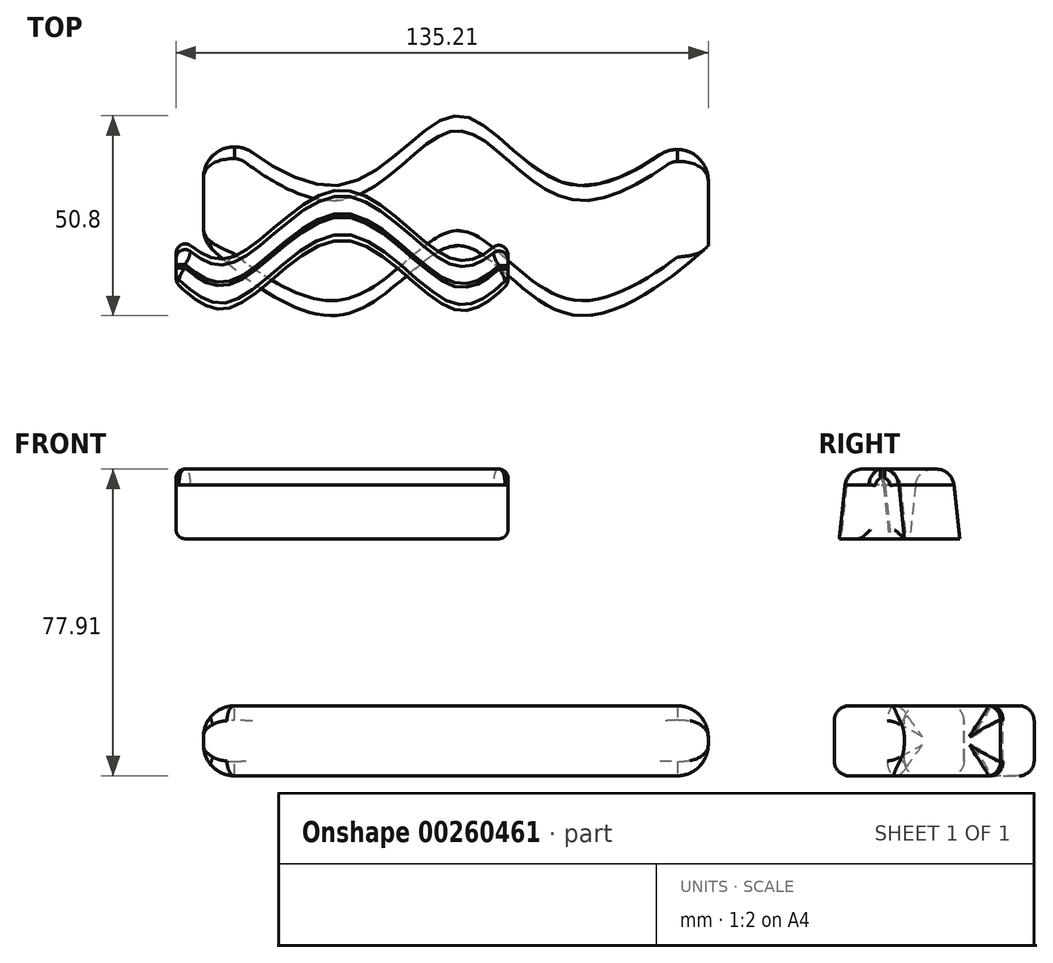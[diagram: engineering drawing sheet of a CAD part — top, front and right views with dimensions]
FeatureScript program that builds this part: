
annotation { "Feature Type Name" : "Feature", "Feature Type Description" : "" }
export const myFeature = defineFeature(function(context is Context, id is Id, definition is map)
    precondition{}
    {
        {
            var Q0;
            Q0=qCreatedBy(makeId("Top.planeOp"),FACE);
            var sketch = newSketch(context, id + "F0", { "sketchPlane" : qUnion([Q0])});
            skLineSegment(sketch, "E0", {"start": v(-76.12, 17.78) * mm, "end": v(-12.62, 17.78) * mm});
            skLineSegment(sketch, "E1", {"start": v(-44.37, 0) * mm, "end": v(19.13, 0) * mm});
            skLineSegment(sketch, "E2", {"start": v(-44.37, 0) * mm, "end": v(-44.37, 17.78) * mm});
            skLineSegment(sketch, "E3", {"start": v(-12.62, 17.78) * mm, "end": v(-12.62, 0) * mm});
            skLineSegment(sketch, "E4", {"start": v(-12.62, 8.9) * mm, "end": v(-44.37, 8.89) * mm});
            skLineSegment(sketch, "E5", {"start": v(-12.62, 17.78) * mm, "end": v(50.88, 17.78) * mm});
            skFitSpline(sketch, "E6", {"points": [v(-77.36, 17.78) * mm, v(-76.12, 17.78) * mm, v(-44.37, 0) * mm, v(-12.62, 17.78) * mm, v(19.13, 0) * mm, v(50.88, 17.78) * mm], "startDerivative": vector(84.4, 0) * mm, "endDerivative": vector(0, 0) * mm});
            skSolve(sketch);
        }
        {
            var Q0;
            Q0=qCreatedBy(makeId("Right.planeOp"),FACE);
            var sketch = newSketch(context, id + "F1", { "sketchPlane" : qUnion([Q0])});
            skLineSegment(sketch, "E7.bottom", {"start": v(-3.81, -40.82) * mm, "end": v(-29.21, -40.82) * mm});
            skLineSegment(sketch, "E7.top", {"start": v(-3.8, -58.6) * mm, "end": v(-29.21, -58.6) * mm});
            skLineSegment(sketch, "E7.left", {"start": v(0, -44.63) * mm, "end": v(0, -54.8) * mm});
            skLineSegment(sketch, "E7.right", {"start": v(-33.02, -44.63) * mm, "end": v(-33.02, -54.8) * mm});
            skPoint(sketch, "E7.middle", {"position": v(-16.51, -49.71) * mm});
            skPoint(sketch, "E8.visualSharp", {"position": v(0, -58.6) * mm});
            skArc(sketch, "E8.filletArc", {"start": v(-3.8, -58.6) * mm, "mid": v(-1.12, -57.49) * mm, "end": v(0, -54.8) * mm});
            skPoint(sketch, "E9.visualSharp", {"position": v(-33.02, -58.6) * mm});
            skArc(sketch, "E9.filletArc", {"start": v(-33.02, -54.8) * mm, "mid": v(-31.9, -57.49) * mm, "end": v(-29.21, -58.6) * mm});
            skPoint(sketch, "E10.visualSharp", {"position": v(-33.02, -40.82) * mm});
            skArc(sketch, "E10.filletArc", {"start": v(-29.21, -40.82) * mm, "mid": v(-31.9, -41.94) * mm, "end": v(-33.02, -44.63) * mm});
            skPoint(sketch, "E11.visualSharp", {"position": v(0, -40.82) * mm});
            skArc(sketch, "E11.filletArc", {"start": v(0, -44.63) * mm, "mid": v(-1.12, -41.94) * mm, "end": v(-3.81, -40.82) * mm});
            skSolve(sketch);
        }
        {
            var Q0;
            Q0=makeQuery(id+"F1.imprint","IMPRINT",FACE,{"disambiguationData":[TD([[makeQuery(id+"F1.imprint","IMPRINT",EDGE,{"derivedFrom":sQuery(id+"F1.wireOp",EDGE,"E7.bottom")}),1.0]])]});
            var Q1;
            Q1=sQuery(id+"F0.wireOp",EDGE,"E6");
            sweep(context, id + "F2", {"profiles" : qUnion([Q0]), "path" : qUnion([Q1]), "keepProfileOrientation" : true});
        }
        {
            var Q0;
            Q0=makeQuery(id+"F2.opSweep","CAP_FACE",FACE,{"disambiguationData":[OSD([sQuery(id+"F0.wireOp",VERTEX,"E6.start"),sQuery(id+"F1.wireOp",EDGE,"E7.bottom"),sQuery(id+"F1.wireOp",EDGE,"E7.top"),sQuery(id+"F1.wireOp",EDGE,"E7.left"),sQuery(id+"F1.wireOp",EDGE,"E7.right"),sQuery(id+"F1.wireOp",EDGE,"E8.filletArc"),sQuery(id+"F1.wireOp",EDGE,"E9.filletArc"),sQuery(id+"F1.wireOp",EDGE,"E10.filletArc"),sQuery(id+"F1.wireOp",EDGE,"E11.filletArc")])],"isStart":false});
            var Q1;
            Q1=makeQuery(id+"F2.opSweep","CAP_FACE",FACE,{"disambiguationData":[OSD([sQuery(id+"F0.wireOp",VERTEX,"E6.end"),sQuery(id+"F1.wireOp",EDGE,"E7.bottom"),sQuery(id+"F1.wireOp",EDGE,"E7.top"),sQuery(id+"F1.wireOp",EDGE,"E7.left"),sQuery(id+"F1.wireOp",EDGE,"E7.right"),sQuery(id+"F1.wireOp",EDGE,"E8.filletArc"),sQuery(id+"F1.wireOp",EDGE,"E9.filletArc"),sQuery(id+"F1.wireOp",EDGE,"E10.filletArc"),sQuery(id+"F1.wireOp",EDGE,"E11.filletArc")])],"isStart":true});
            fillet(context, id + "F3", {"entities" : qUnion([Q0, Q1]), "radius" : 7.87 * mm, "tangentPropagation" : true, "allowEdgeOverflow" : false});
        }
        {
            var Q0;
            Q0=makeQuery(id+"F2.opSweep","SWEPT_FACE",FACE,{"disambiguationData":[OSD([sQuery(id+"F0.wireOp",EDGE,"E6"),sQuery(id+"F1.wireOp",EDGE,"E7.top")])]});
            var sketch = newSketch(context, id + "F4", { "sketchPlane" : qUnion([Q0])});
            skLineSegment(sketch, "E12", {"start": v(-120.37, 23.01) * mm, "end": v(-7.87, 23.01) * mm});
            skLineSegment(sketch, "E13", {"start": v(-64.12, 23.01) * mm, "end": v(-64.12, 3.83) * mm});
            skPoint(sketch, "E14", {"position": v(-92.25, 23.01) * mm});
            skPoint(sketch, "E15", {"position": v(-36, 23.01) * mm});
            skLineSegment(sketch, "E16", {"start": v(-120.37, 35.1) * mm, "end": v(-7.87, 35.93) * mm});
            skLineSegment(sketch, "E17", {"start": v(-92.25, 23.01) * mm, "end": v(-92.25, 35.31) * mm});
            skLineSegment(sketch, "E18", {"start": v(-36, 23.01) * mm, "end": v(-36, 35.73) * mm});
            skPoint(sketch, "E19", {"position": v(-106.3, 23.01) * mm});
            skPoint(sketch, "E20", {"position": v(-21.93, 23.01) * mm});
            skLineSegment(sketch, "E21", {"start": v(-21.93, 23.01) * mm, "end": v(-22.03, 35.83) * mm});
            skLineSegment(sketch, "E22", {"start": v(-106.3, 23.01) * mm, "end": v(-106.3, 35.2) * mm});
            skPoint(sketch, "E23", {"position": v(-106.3, 29.1) * mm});
            skPoint(sketch, "E24", {"position": v(-21.98, 29.42) * mm});
            skPoint(sketch, "E25", {"position": v(-64.12, 13.42) * mm});
            skLineSegment(sketch, "E26", {"start": v(-64.12, 13.42) * mm, "end": v(-64.12, 23.01) * mm});
            skPoint(sketch, "E27", {"position": v(-64.12, 18.22) * mm});
            skFitSpline(sketch, "E28", {"points": [v(-106.3, 29.1) * mm, v(-92.25, 35.31) * mm, v(-64.12, 18.22) * mm, v(-36, 35.73) * mm, v(-21.98, 29.42) * mm], "startDerivative": vector(64.15, 58.57) * mm, "endDerivative": vector(63.99, -59.4) * mm});
            skSolve(sketch);
        }
        {
            var Q0;
            Q0=qCreatedBy(makeId("Right.planeOp"),FACE);
            var sketch = newSketch(context, id + "F5", { "sketchPlane" : qUnion([Q0])});
            skLineSegment(sketch, "E29", {"start": v(-22.58, 1.63) * mm, "end": v(-35.28, 1.63) * mm});
            skLineSegment(sketch, "E30", {"start": v(-28.48, 19.3) * mm, "end": v(-29.39, 19.3) * mm});
            skLineSegment(sketch, "E31", {"start": v(-24.06, 15.34) * mm, "end": v(-22.58, 1.63) * mm});
            skLineSegment(sketch, "E32", {"start": v(-33.8, 15.34) * mm, "end": v(-35.28, 1.63) * mm});
            skPoint(sketch, "E33.visualSharp", {"position": v(-33.38, 19.3) * mm});
            skArc(sketch, "E33.filletArc", {"start": v(-29.39, 19.3) * mm, "mid": v(-32.36, 18.17) * mm, "end": v(-33.8, 15.34) * mm});
            skPoint(sketch, "E34.visualSharp", {"position": v(-24.49, 19.3) * mm});
            skArc(sketch, "E34.filletArc", {"start": v(-24.06, 15.34) * mm, "mid": v(-25.5, 18.17) * mm, "end": v(-28.48, 19.3) * mm});
            skSolve(sketch);
        }
        {
            var Q0;
            Q0=makeQuery(id+"F5.imprint","IMPRINT",FACE,{"disambiguationData":[TD([[makeQuery(id+"F5.imprint","IMPRINT",EDGE,{"derivedFrom":sQuery(id+"F5.wireOp",EDGE,"E29")}),-1.0]])]});
            var Q1;
            Q1=sQuery(id+"F4.wireOp",EDGE,"E28");
            sweep(context, id + "F6", {"profiles" : qUnion([Q0]), "path" : qUnion([Q1]), "keepProfileOrientation" : true});
        }
        {
            var Q0;
            Q0=makeQuery(id+"F6.opSweep","CAP_FACE",FACE,{"disambiguationData":[OSD([sQuery(id+"F4.wireOp",VERTEX,"E28.start"),sQuery(id+"F5.wireOp",EDGE,"E29"),sQuery(id+"F5.wireOp",EDGE,"E30"),sQuery(id+"F5.wireOp",EDGE,"E31"),sQuery(id+"F5.wireOp",EDGE,"E32"),sQuery(id+"F5.wireOp",EDGE,"E33.filletArc"),sQuery(id+"F5.wireOp",EDGE,"E34.filletArc")])],"isStart":false});
            var Q1;
            Q1=makeQuery(id+"F6.opSweep","CAP_FACE",FACE,{"disambiguationData":[OSD([sQuery(id+"F4.wireOp",VERTEX,"E28.end"),sQuery(id+"F5.wireOp",EDGE,"E29"),sQuery(id+"F5.wireOp",EDGE,"E30"),sQuery(id+"F5.wireOp",EDGE,"E31"),sQuery(id+"F5.wireOp",EDGE,"E32"),sQuery(id+"F5.wireOp",EDGE,"E33.filletArc"),sQuery(id+"F5.wireOp",EDGE,"E34.filletArc")])],"isStart":true});
            fillet(context, id + "F7", {"entities" : qUnion([Q0, Q1]), "radius" : 2.3 * mm, "tangentPropagation" : true, "allowEdgeOverflow" : false});
        }
    });
